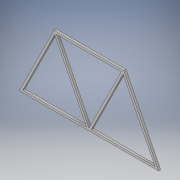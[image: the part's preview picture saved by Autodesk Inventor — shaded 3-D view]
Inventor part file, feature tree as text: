
AUTODESK INVENTOR PART (.ipt)
format: ipt  version: 2016 (Build 200138000, 138)  size: 117,248 bytes
history: native  units: in
note: dims shown in document units (in); Inventor stores cm internally (conversion verified against a paired STEP export)
features: extrude x1, sketch x1
ambient origin geometry x8: Origin, YZ Plane, XZ Plane, XY Plane, X Axis, Y Axis, Z Axis, Center Point
bodies: Body1 (feature_tree)
feature tree (2):
  extrude  "Extrusion2"  Depth=0.125in
  sketch  "Sketch1"  dims[d0=8.0in d40=0.125in d42=0.125in d44=0.125in d45=0.125in d51=4.0in d52=3.6799in d53=3.7207in d54=3.8056in d55=0.125in d56=0.0in]
